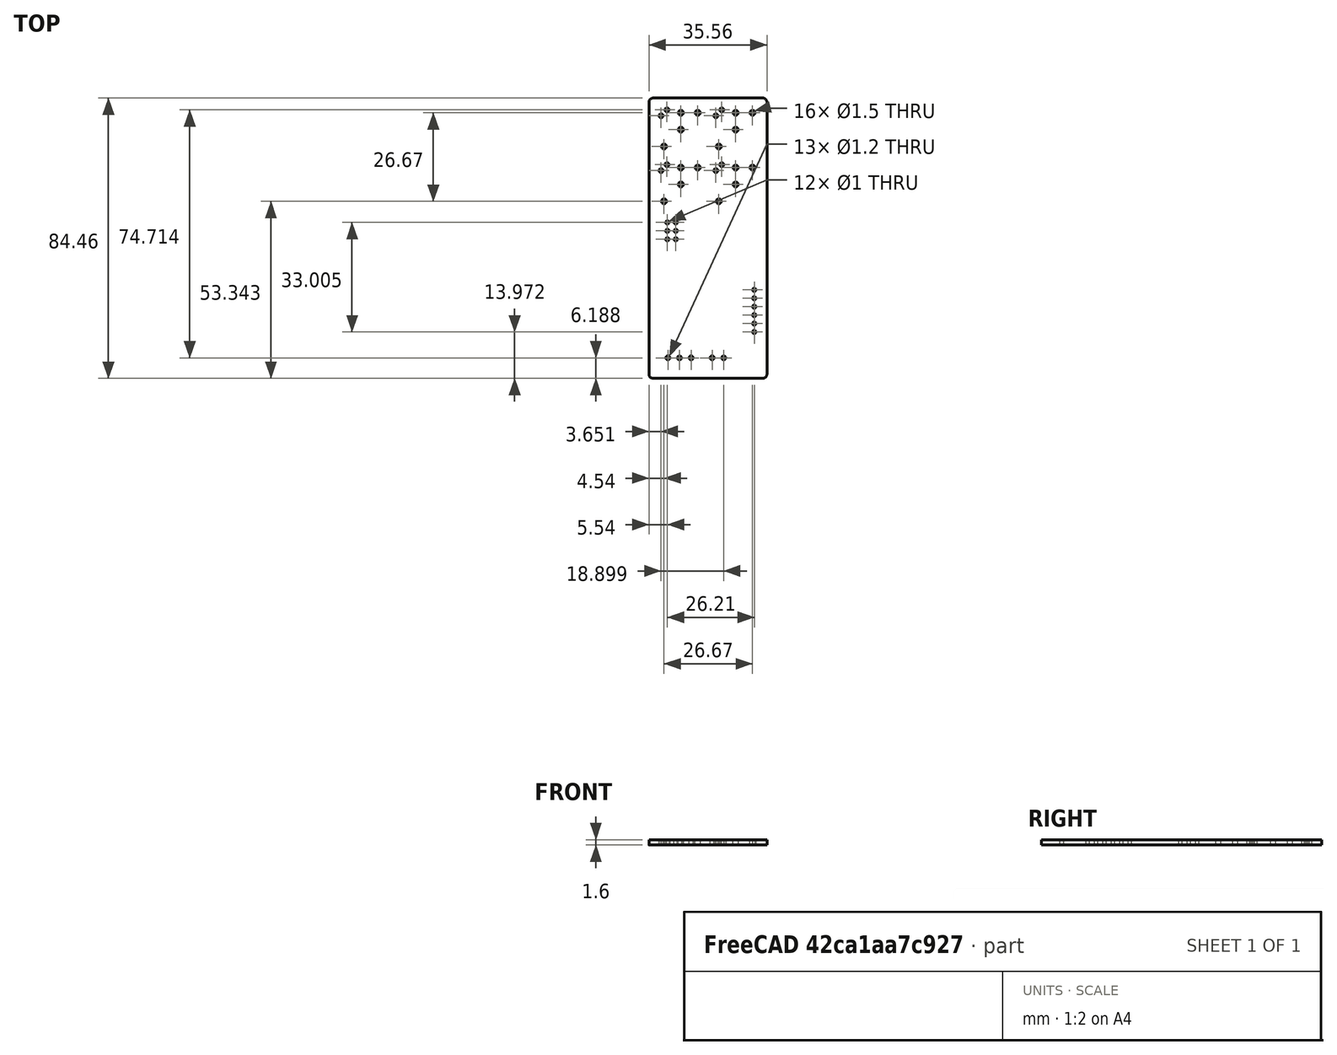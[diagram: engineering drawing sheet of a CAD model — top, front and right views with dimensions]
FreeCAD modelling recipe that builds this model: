
FCSTD DOCUMENT  (FreeCAD 0.20R29177 +426 (Git))
Label: doboz_v1
License: All rights reserved
LicenseURL: http://en.wikipedia.org/wiki/All_rights_reserved
objects: App::Part×4, Sketcher::SketchObject×2, PartDesign::CoordinateSystem×1, Part::Feature×1, PartDesign::Body×1
note: 5 computed .brp shape members not serialized (recipe doc carries the construction recipe); baked Part::Feature solids carry a one-line shape summary decoded from their .brp

FEATURE [PartDesign::CoordinateSystem] Local_CS_c95c
  AttacherType = Attacher::AttachEngine3D
  MapMode = 2
  Support = -> [X_Axis001]
FEATURE [Sketcher::SketchObject] PCB_Sketch_c95c
  FullyConstrained = false
  sketch-geometry (8):
    g0: LineSegment StartX=128.905 StartY=-49.53 StartZ=0 EndX=161.925 EndY=-49.53 EndZ=0
    g1: LineSegment StartX=163.195 StartY=-50.8 StartZ=0 EndX=163.195 EndY=-132.715 EndZ=0
    g2: LineSegment StartX=161.925 StartY=-133.985 StartZ=0 EndX=128.905 EndY=-133.985 EndZ=0
    g3: LineSegment StartX=127.635 StartY=-132.715 StartZ=0 EndX=127.635 EndY=-50.8 EndZ=0
    g4: ArcOfCircle CenterX=161.925 CenterY=-132.715 CenterZ=0 NormalX=0 NormalY=0 NormalZ=-1 AngleXU=3.14159 Radius=1.27 StartAngle=0 EndAngle=1.5708
    g5: ArcOfCircle CenterX=161.925 CenterY=-50.8 CenterZ=0 NormalX=0 NormalY=0 NormalZ=-1 AngleXU=1.5708 Radius=1.27 StartAngle=0 EndAngle=1.5708
    g6: ArcOfCircle CenterX=128.905 CenterY=-132.715 CenterZ=0 NormalX=0 NormalY=0 NormalZ=-1 AngleXU=-1.5708 Radius=1.27 StartAngle=0 EndAngle=1.5708
    g7: ArcOfCircle CenterX=128.905 CenterY=-50.8 CenterZ=0 NormalX=0 NormalY=0 NormalZ=-1 AngleXU=-1.04279e-06 Radius=1.27 StartAngle=0 EndAngle=1.5708
  constraints (8):
    c: Coincident(g3,g6)
    c: Coincident(g3,g7)
    c: Coincident(g2,g6)
    c: Coincident(g0,g7)
    c: Coincident(g2,g4)
    c: Coincident(g0,g5)
    c: Coincident(g1,g4)
    c: Coincident(g1,g5)
FEATURE [App::Part] Board_Geoms_c95c
  Group = -> [PCB_Sketch_c95c]
  Origin = -> Origin
FEATURE [App::Part] Step_Models_c95c
  Origin = -> Origin002
FEATURE [App::Part] Board_c95c  label="SEM_ProjektoroSCH-Rev2"
  Group = -> [Local_CS_c95c,Board_Geoms_c95c,Step_Models_c95c]
  Origin = -> Origin001
FEATURE [Part::Feature] Shape  label="Pcb_c95c"
  shape: bbox 35.56 x 84.46 x 1.6 mm, 51 faces (baked)
FEATURE [Sketcher::SketchObject] Sketch
  FullyConstrained = false
  MapMode = 5
  Support = -> [XY_Plane004]
  sketch-geometry (4):
    g0: LineSegment StartX=-88.5933 StartY=67.2415 StartZ=0 EndX=-52.5933 EndY=67.2415 EndZ=0
    g1: LineSegment StartX=-52.5933 StartY=67.2415 StartZ=0 EndX=-52.5933 EndY=-18.7585 EndZ=0
    g2: LineSegment StartX=-52.5933 StartY=-18.7585 StartZ=0 EndX=-88.5933 EndY=-18.7585 EndZ=0
    g3: LineSegment StartX=-88.5933 StartY=-18.7585 StartZ=0 EndX=-88.5933 EndY=67.2415 EndZ=0
  constraints (10):
    c: Coincident(g0,g1)
    c: Coincident(g1,g2)
    c: Coincident(g2,g3)
    c: Coincident(g3,g0)
    c: Horizontal(g0)
    c: Horizontal(g2)
    c: Vertical(g1)
    c: Vertical(g3)
    c: DistanceX(g0,g0) = 36
    c: DistanceY(g1,g1) = 86
FEATURE [PartDesign::Body] Body  label="Case"
  Group = -> [Sketch]
  Origin = -> Origin004
FEATURE [App::Part] Part  label="Doboz"
  Group = -> [Body]
  Origin = -> Origin003
